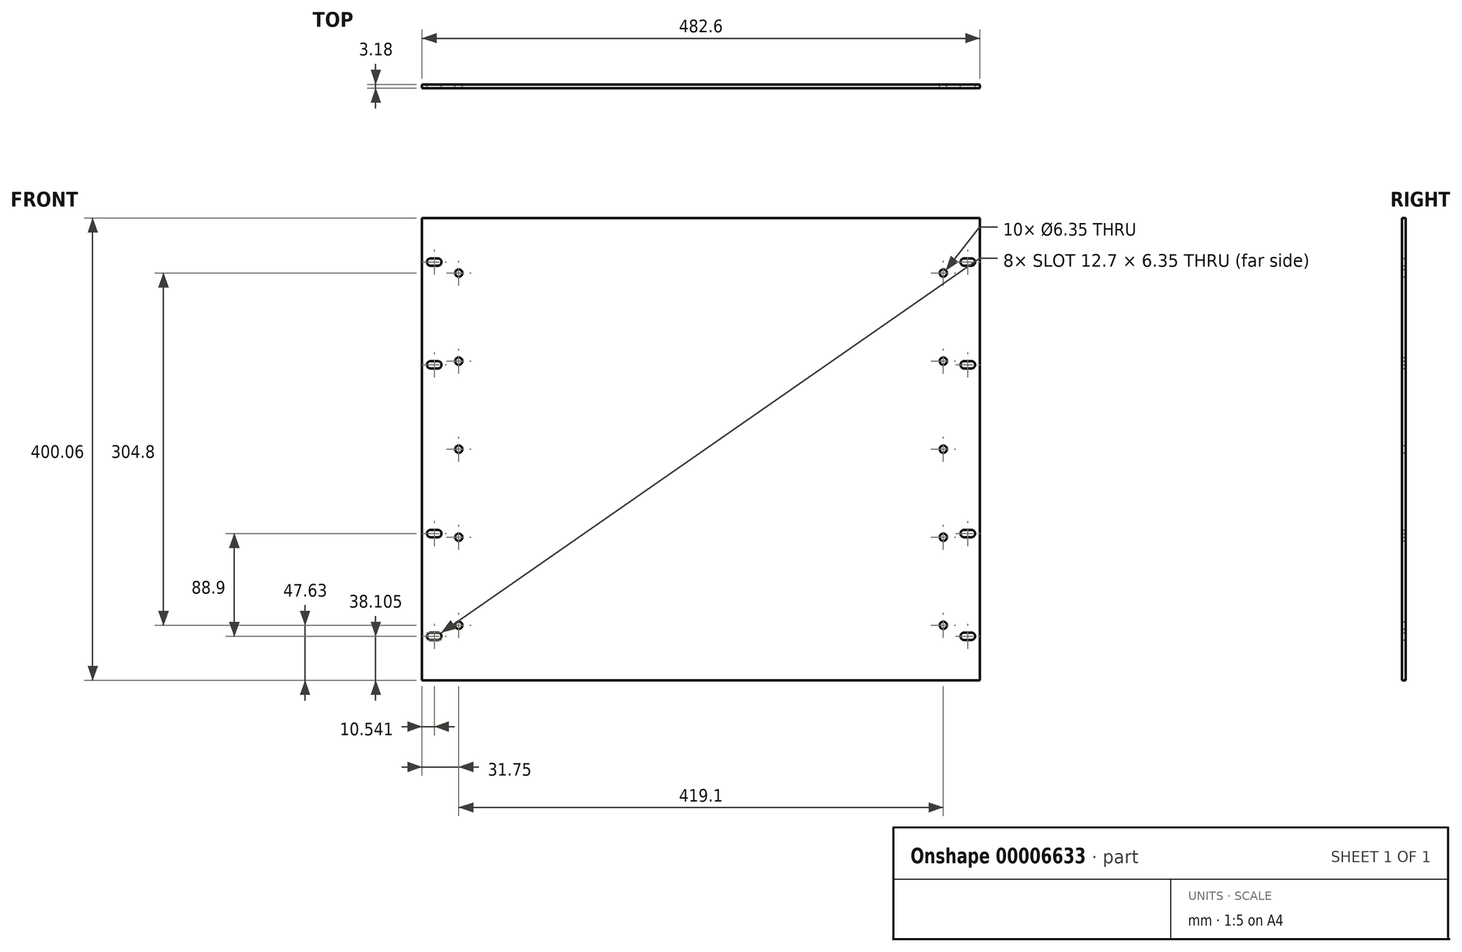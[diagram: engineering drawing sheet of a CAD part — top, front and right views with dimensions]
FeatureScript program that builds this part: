
annotation { "Feature Type Name" : "Feature", "Feature Type Description" : "" }
export const myFeature = defineFeature(function(context is Context, id is Id, definition is map)
    precondition{}
    {
        {
            var Q0;
            Q0=qCreatedBy(makeId("Front.planeOp"),FACE);
            var sketch = newSketch(context, id + "F0", { "sketchPlane" : qUnion([Q0])});
            skLineSegment(sketch, "E0.rect.bottom", {"start": v(241.3, 200.03) * mm, "end": v(-241.3, 200.02) * mm});
            skLineSegment(sketch, "E0.rect.top", {"start": v(241.3, -200.03) * mm, "end": v(-241.3, -200.03) * mm});
            skLineSegment(sketch, "E0.rect.left", {"start": v(241.3, 200.03) * mm, "end": v(241.3, -200.03) * mm});
            skLineSegment(sketch, "E0.rect.right", {"start": v(-241.3, 200.02) * mm, "end": v(-241.3, -200.03) * mm});
            skPoint(sketch, "E0.rect.middle", {"position": v(0, 0) * mm});
            skLineSegment(sketch, "E1", {"start": v(-286.23, 161.92) * mm, "end": v(258.94, 161.93) * mm, "construction": true});
            skLineSegment(sketch, "E2", {"start": v(-287.5, 73.02) * mm, "end": v(258.3, 73.03) * mm, "construction": true});
            skArc(sketch, "E3", {"start": v(233.93, 158.75) * mm, "mid": v(237.1, 161.92) * mm, "end": v(233.93, 165.1) * mm});
            skArc(sketch, "E4", {"start": v(227.58, 165.1) * mm, "mid": v(224.4, 161.92) * mm, "end": v(227.58, 158.75) * mm});
            skLineSegment(sketch, "E5", {"start": v(227.58, 165.1) * mm, "end": v(233.93, 165.1) * mm});
            skLineSegment(sketch, "E6", {"start": v(227.58, 158.75) * mm, "end": v(233.93, 158.75) * mm});
            skLineSegment(sketch, "E7", {"start": v(247.3, 161.93) * mm, "end": v(247.3, 73.03) * mm, "construction": true});
            skLineSegment(sketch, "E8", {"start": v(247.3, 117.48) * mm, "end": v(204.83, 117.48) * mm, "construction": true});
            skLineSegment(sketch, "E9", {"start": v(-288.37, 0) * mm, "end": v(260.54, 0) * mm, "construction": true});
            skLineSegment(sketch, "E10", {"start": v(0, 213.9) * mm, "end": v(0, -209.66) * mm, "construction": true});
            skArc(sketch, "E11.0.MirrorCS", {"start": v(227.58, 69.85) * mm, "mid": v(224.4, 73.03) * mm, "end": v(227.58, 76.2) * mm});
            skLineSegment(sketch, "E12.0.MirrorCS", {"start": v(227.58, 69.85) * mm, "end": v(233.93, 69.85) * mm});
            skArc(sketch, "E13.0.MirrorCS", {"start": v(233.93, 76.2) * mm, "mid": v(237.1, 73.03) * mm, "end": v(233.93, 69.85) * mm});
            skLineSegment(sketch, "E14.0.MirrorCS", {"start": v(227.58, 76.2) * mm, "end": v(233.93, 76.2) * mm});
            skLineSegment(sketch, "E15.0.MirrorCS", {"start": v(227.58, -165.1) * mm, "end": v(233.93, -165.1) * mm});
            skLineSegment(sketch, "E15.1.MirrorCS", {"start": v(227.58, -158.75) * mm, "end": v(233.93, -158.75) * mm});
            skArc(sketch, "E15.2.MirrorCS", {"start": v(227.58, -165.1) * mm, "mid": v(224.4, -161.92) * mm, "end": v(227.58, -158.75) * mm});
            skArc(sketch, "E15.3.MirrorCS", {"start": v(233.93, -158.75) * mm, "mid": v(237.1, -161.92) * mm, "end": v(233.93, -165.1) * mm});
            skLineSegment(sketch, "E16.0.MirrorCS", {"start": v(227.58, -69.85) * mm, "end": v(233.93, -69.85) * mm});
            skLineSegment(sketch, "E16.1.MirrorCS", {"start": v(227.58, -76.2) * mm, "end": v(233.93, -76.2) * mm});
            skArc(sketch, "E16.2.MirrorCS", {"start": v(227.58, -69.85) * mm, "mid": v(224.4, -73.03) * mm, "end": v(227.58, -76.2) * mm});
            skLineSegment(sketch, "E16.3.MirrorCS", {"start": v(227.58, -69.85) * mm, "end": v(233.93, -69.85) * mm});
            skArc(sketch, "E16.4.MirrorCS", {"start": v(233.93, -76.2) * mm, "mid": v(237.1, -73.03) * mm, "end": v(233.93, -69.85) * mm});
            skLineSegment(sketch, "E16.5.MirrorCS", {"start": v(227.58, -76.2) * mm, "end": v(233.93, -76.2) * mm});
            skArc(sketch, "E16.6.MirrorCS", {"start": v(233.93, -76.2) * mm, "mid": v(237.1, -73.03) * mm, "end": v(233.93, -69.85) * mm});
            skArc(sketch, "E16.7.MirrorCS", {"start": v(227.58, -69.85) * mm, "mid": v(224.4, -73.03) * mm, "end": v(227.58, -76.2) * mm});
            skLineSegment(sketch, "E16.8.MirrorCS", {"start": v(227.58, -76.2) * mm, "end": v(233.93, -76.2) * mm});
            skLineSegment(sketch, "E16.9.MirrorCS", {"start": v(227.58, -69.85) * mm, "end": v(233.93, -69.85) * mm});
            skArc(sketch, "E16.10.MirrorCS", {"start": v(233.93, -76.2) * mm, "mid": v(237.1, -73.03) * mm, "end": v(233.93, -69.85) * mm});
            skArc(sketch, "E16.11.MirrorCS", {"start": v(227.58, -69.85) * mm, "mid": v(224.4, -73.03) * mm, "end": v(227.58, -76.2) * mm});
            skLineSegment(sketch, "E17.0.MirrorCS", {"start": v(-227.58, 76.2) * mm, "end": v(-233.93, 76.2) * mm});
            skLineSegment(sketch, "E17.1.MirrorCS", {"start": v(-227.58, 69.85) * mm, "end": v(-233.93, 69.85) * mm});
            skArc(sketch, "E17.2.MirrorCS", {"start": v(-227.58, 69.85) * mm, "mid": v(-224.4, 73.03) * mm, "end": v(-227.58, 76.2) * mm});
            skLineSegment(sketch, "E17.3.MirrorCS", {"start": v(-227.58, 76.2) * mm, "end": v(-233.93, 76.2) * mm});
            skArc(sketch, "E17.4.MirrorCS", {"start": v(-233.93, 76.2) * mm, "mid": v(-237.1, 73.03) * mm, "end": v(-233.93, 69.85) * mm});
            skLineSegment(sketch, "E17.5.MirrorCS", {"start": v(-227.58, 69.85) * mm, "end": v(-233.93, 69.85) * mm});
            skArc(sketch, "E17.6.MirrorCS", {"start": v(-227.58, 69.85) * mm, "mid": v(-224.4, 73.03) * mm, "end": v(-227.58, 76.2) * mm});
            skArc(sketch, "E17.7.MirrorCS", {"start": v(-233.93, 76.2) * mm, "mid": v(-237.1, 73.03) * mm, "end": v(-233.93, 69.85) * mm});
            skArc(sketch, "E17.8.MirrorCS", {"start": v(-227.58, 69.85) * mm, "mid": v(-224.4, 73.03) * mm, "end": v(-227.58, 76.2) * mm});
            skLineSegment(sketch, "E17.9.MirrorCS", {"start": v(-227.58, 69.85) * mm, "end": v(-233.93, 69.85) * mm});
            skArc(sketch, "E17.10.MirrorCS", {"start": v(-233.93, 76.2) * mm, "mid": v(-237.1, 73.03) * mm, "end": v(-233.93, 69.85) * mm});
            skLineSegment(sketch, "E17.11.MirrorCS", {"start": v(-227.58, 76.2) * mm, "end": v(-233.93, 76.2) * mm});
            skArc(sketch, "E17.12.MirrorCS", {"start": v(-233.93, 158.75) * mm, "mid": v(-237.1, 161.92) * mm, "end": v(-233.93, 165.1) * mm});
            skLineSegment(sketch, "E17.13.MirrorCS", {"start": v(-227.58, 158.75) * mm, "end": v(-233.93, 158.75) * mm});
            skLineSegment(sketch, "E17.14.MirrorCS", {"start": v(-227.58, 165.1) * mm, "end": v(-233.93, 165.1) * mm});
            skArc(sketch, "E17.15.MirrorCS", {"start": v(-227.58, 165.1) * mm, "mid": v(-224.4, 161.92) * mm, "end": v(-227.58, 158.75) * mm});
            skLineSegment(sketch, "E17.16.MirrorCS", {"start": v(-227.58, -76.2) * mm, "end": v(-233.93, -76.2) * mm});
            skLineSegment(sketch, "E17.17.MirrorCS", {"start": v(-227.58, -69.85) * mm, "end": v(-233.93, -69.85) * mm});
            skArc(sketch, "E17.18.MirrorCS", {"start": v(-233.93, -76.2) * mm, "mid": v(-237.1, -73.03) * mm, "end": v(-233.93, -69.85) * mm});
            skLineSegment(sketch, "E17.19.MirrorCS", {"start": v(-227.58, -69.85) * mm, "end": v(-233.93, -69.85) * mm});
            skArc(sketch, "E17.20.MirrorCS", {"start": v(-227.58, -69.85) * mm, "mid": v(-224.4, -73.03) * mm, "end": v(-227.58, -76.2) * mm});
            skLineSegment(sketch, "E17.21.MirrorCS", {"start": v(-227.58, -76.2) * mm, "end": v(-233.93, -76.2) * mm});
            skArc(sketch, "E17.22.MirrorCS", {"start": v(-233.93, -76.2) * mm, "mid": v(-237.1, -73.03) * mm, "end": v(-233.93, -69.85) * mm});
            skArc(sketch, "E17.23.MirrorCS", {"start": v(-227.58, -69.85) * mm, "mid": v(-224.4, -73.03) * mm, "end": v(-227.58, -76.2) * mm});
            skArc(sketch, "E17.24.MirrorCS", {"start": v(-233.93, -76.2) * mm, "mid": v(-237.1, -73.03) * mm, "end": v(-233.93, -69.85) * mm});
            skLineSegment(sketch, "E17.25.MirrorCS", {"start": v(-227.58, -69.85) * mm, "end": v(-233.93, -69.85) * mm});
            skArc(sketch, "E17.26.MirrorCS", {"start": v(-227.58, -69.85) * mm, "mid": v(-224.4, -73.03) * mm, "end": v(-227.58, -76.2) * mm});
            skLineSegment(sketch, "E17.27.MirrorCS", {"start": v(-227.58, -76.2) * mm, "end": v(-233.93, -76.2) * mm});
            skArc(sketch, "E17.28.MirrorCS", {"start": v(-227.58, -165.1) * mm, "mid": v(-224.4, -161.92) * mm, "end": v(-227.58, -158.75) * mm});
            skLineSegment(sketch, "E17.29.MirrorCS", {"start": v(-227.58, -165.1) * mm, "end": v(-233.93, -165.1) * mm});
            skLineSegment(sketch, "E17.30.MirrorCS", {"start": v(-227.58, -158.75) * mm, "end": v(-233.93, -158.75) * mm});
            skArc(sketch, "E17.31.MirrorCS", {"start": v(-233.93, -158.75) * mm, "mid": v(-237.1, -161.92) * mm, "end": v(-233.93, -165.1) * mm});
            skLineSegment(sketch, "E18", {"start": v(-209.55, 213.9) * mm, "end": v(-209.55, -215.97) * mm, "construction": true});
            skCircle(sketch, "E19", {"center": v(-209.55, 76.2) * mm, "radius": 3.18 * mm});
            skCircle(sketch, "E20", {"center": v(-209.55, 152.4) * mm, "radius": 3.18 * mm});
            skCircle(sketch, "E21", {"center": v(-209.55, 0) * mm, "radius": 3.18 * mm});
            skCircle(sketch, "E22", {"center": v(-209.55, -76.2) * mm, "radius": 3.18 * mm});
            skCircle(sketch, "E23", {"center": v(-209.55, -152.4) * mm, "radius": 3.18 * mm});
            skCircle(sketch, "E24.0.MirrorC", {"center": v(209.55, 152.4) * mm, "radius": 3.18 * mm});
            skCircle(sketch, "E25.0.MirrorC", {"center": v(209.55, 76.2) * mm, "radius": 3.18 * mm});
            skCircle(sketch, "E26.0.MirrorC", {"center": v(209.55, 0) * mm, "radius": 3.18 * mm});
            skCircle(sketch, "E27.0.MirrorC", {"center": v(209.55, -76.2) * mm, "radius": 3.18 * mm});
            skCircle(sketch, "E28.0.MirrorC", {"center": v(209.55, -152.4) * mm, "radius": 3.18 * mm});
            skSolve(sketch);
        }
        {
            var Q0;
            Q0=makeQuery(id+"F0.imprint","IMPRINT",FACE,{"disambiguationData":[TD([[makeQuery(id+"F0.imprint","IMPRINT",EDGE,{"derivedFrom":sQuery(id+"F0.wireOp",EDGE,"E0.rect.bottom")}),1.0]])]});
            extrude(context, id + "F1", {"entities" : qUnion([Q0]), "depth" : 3.17 * mm});
        }
    });
